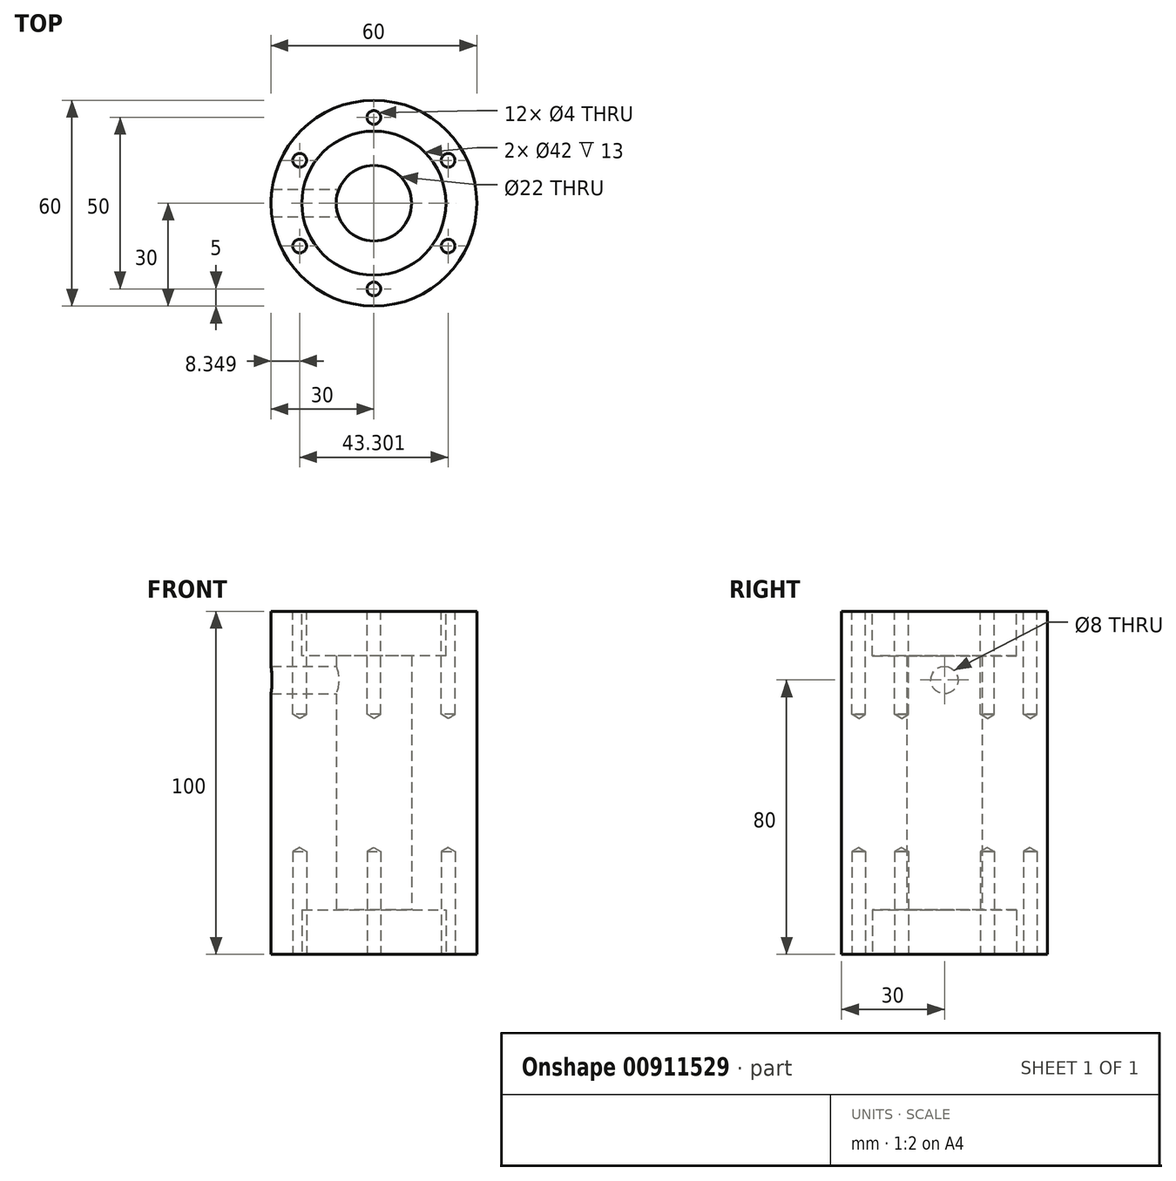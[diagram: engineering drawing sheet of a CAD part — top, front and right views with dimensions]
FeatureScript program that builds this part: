
annotation { "Feature Type Name" : "Feature", "Feature Type Description" : "" }
export const myFeature = defineFeature(function(context is Context, id is Id, definition is map)
    precondition{}
    {
        {
            var Q0;
            Q0=qCreatedBy(makeId("Top.planeOp"),FACE);
            var sketch = newSketch(context, id + "F0", { "sketchPlane" : qUnion([Q0])});
            skCircle(sketch, "E0", {"center": v(0, 0) * mm, "radius": 11 * mm});
            skCircle(sketch, "E1", {"center": v(0, 0) * mm, "radius": 30 * mm});
            skSolve(sketch);
        }
        {
            var Q0;
            Q0=makeQuery(id+"F0.imprint","IMPRINT",FACE,{"disambiguationData":[TD([[makeQuery(id+"F0.imprint","IMPRINT",EDGE,{"derivedFrom":sQuery(id+"F0.wireOp",EDGE,"E0")}),-1.0]])]});
            extrude(context, id + "F1", {"entities" : qUnion([Q0]), "depth" : 100 * mm, "offsetDistance" : 25 * mm});
        }
        {
            var Q0;
            Q0=makeQuery(id+"F1.opExtrude","CAP_FACE",FACE,{"disambiguationData":[OSD([sQuery(id+"F0.wireOp",EDGE,"E0"),sQuery(id+"F0.wireOp",EDGE,"E1")])],"isStart":false});
            var sketch = newSketch(context, id + "F2", { "sketchPlane" : qUnion([Q0])});
            skCircle(sketch, "E2", {"center": v(0, 0) * mm, "radius": 21 * mm});
            skCircle(sketch, "E3", {"center": v(0, 0) * mm, "radius": 11 * mm});
            skSolve(sketch);
        }
        {
            var Q0;
            Q0=makeQuery(id+"F2.imprint","IMPRINT",FACE,{"disambiguationData":[TD([[makeQuery(id+"F2.imprint","IMPRINT",EDGE,{"derivedFrom":sQuery(id+"F2.wireOp",EDGE,"E2")}),1.0]])]});
            extrude(context, id + "F3", {"entities" : qUnion([Q0]), "operationType" : NewBodyOperationType.REMOVE, "oppositeDirection" : true, "depth" : 13 * mm, "offsetDistance" : 25 * mm});
        }
        {
            var Q0;
            Q0=makeQuery(id+"F1.opExtrude","CAP_FACE",FACE,{"disambiguationData":[OSD([sQuery(id+"F0.wireOp",EDGE,"E0"),sQuery(id+"F0.wireOp",EDGE,"E1")])],"isStart":true});
            var sketch = newSketch(context, id + "F4", { "sketchPlane" : qUnion([Q0])});
            skCircle(sketch, "E4", {"center": v(0, 0) * mm, "radius": 21 * mm});
            skCircle(sketch, "E5", {"center": v(0, 0) * mm, "radius": 11 * mm});
            skSolve(sketch);
        }
        {
            var Q0;
            Q0=makeQuery(id+"F4.imprint","IMPRINT",FACE,{"disambiguationData":[TD([[makeQuery(id+"F4.imprint","IMPRINT",EDGE,{"derivedFrom":sQuery(id+"F4.wireOp",EDGE,"E4")}),1.0]])]});
            extrude(context, id + "F5", {"entities" : qUnion([Q0]), "operationType" : NewBodyOperationType.REMOVE, "oppositeDirection" : true, "depth" : 13 * mm, "offsetDistance" : 25 * mm});
        }
        {
            var Q0;
            Q0=qCreatedBy(makeId("Right.planeOp"),FACE);
            var sketch = newSketch(context, id + "F6", { "sketchPlane" : qUnion([Q0])});
            skPoint(sketch, "E6", {"position": v(0, 80) * mm});
            skSolve(sketch);
        }
        {
            var Q0;
            Q0=sQuery(id+"F6.wireOp",VERTEX,"E6");
            var Q1;
            Q1=makeQuery(id+"F1.opExtrude","SWEPT_BODY",BODY,{"disambiguationData":[OSD([sQuery(id+"F0.wireOp",EDGE,"E0"),sQuery(id+"F0.wireOp",EDGE,"E1")])]});
            hole(context, id + "F7", {"style" : HoleStyle.SIMPLE, "endStyle" : HoleEndStyle.THROUGH, "holeDiameter" : 8 * mm, "majorDiameter" : 5 * mm, "isTappedThrough" : true, "tappedDepth" : 12 * mm, "tapClearance" : 3, "locations" : qUnion([Q0]), "scope" : qUnion([Q1])});
        }
        {
            var Q0;
            Q0=makeQuery(id+"F1.opExtrude","CAP_FACE",FACE,{"disambiguationData":[OSD([sQuery(id+"F0.wireOp",EDGE,"E0"),sQuery(id+"F0.wireOp",EDGE,"E1")])],"isStart":false});
            var sketch = newSketch(context, id + "F8", { "sketchPlane" : qUnion([Q0])});
            skPoint(sketch, "E7", {"position": v(0, 25) * mm});
            skPoint(sketch, "E8.1.0", {"position": v(-21.65, 12.5) * mm});
            skPoint(sketch, "E8.2.0", {"position": v(-21.65, -12.5) * mm});
            skPoint(sketch, "E8.3.0", {"position": v(0, -25) * mm});
            skPoint(sketch, "E8.4.0", {"position": v(21.65, -12.5) * mm});
            skPoint(sketch, "E8.5.0", {"position": v(21.65, 12.5) * mm});
            skPoint(sketch, "E8.center", {"position": v(0, 0) * mm});
            skSolve(sketch);
        }
        {
            var Q0;
            Q0=sQuery(id+"F8.wireOp",VERTEX,"E7");
            var Q1;
            Q1=sQuery(id+"F8.wireOp",VERTEX,"E8.5.0");
            var Q2;
            Q2=sQuery(id+"F8.wireOp",VERTEX,"E8.4.0");
            var Q3;
            Q3=sQuery(id+"F8.wireOp",VERTEX,"E8.3.0");
            var Q4;
            Q4=sQuery(id+"F8.wireOp",VERTEX,"E8.2.0");
            var Q5;
            Q5=sQuery(id+"F8.wireOp",VERTEX,"E8.1.0");
            var Q6;
            Q6=makeQuery(id+"F1.opExtrude","SWEPT_BODY",BODY,{"disambiguationData":[OSD([sQuery(id+"F0.wireOp",EDGE,"E0"),sQuery(id+"F0.wireOp",EDGE,"E1")])]});
            hole(context, id + "F9", {"style" : HoleStyle.SIMPLE, "endStyle" : HoleEndStyle.BLIND, "holeDiameter" : 4 * mm, "majorDiameter" : 5 * mm, "holeDepth" : 30 * mm, "isTappedThrough" : true, "tappedDepth" : 12 * mm, "tapClearance" : 3, "locations" : qUnion([Q0, Q1, Q2, Q3, Q4, Q5]), "scope" : qUnion([Q6])});
        }
        {
            var Q0;
            Q0=makeQuery(id+"F1.opExtrude","CAP_FACE",FACE,{"disambiguationData":[OSD([sQuery(id+"F0.wireOp",EDGE,"E0"),sQuery(id+"F0.wireOp",EDGE,"E1")])],"isStart":true});
            var sketch = newSketch(context, id + "F10", { "sketchPlane" : qUnion([Q0])});
            skPoint(sketch, "E9", {"position": v(0, 25) * mm});
            skPoint(sketch, "E10.1.0", {"position": v(-21.65, 12.5) * mm});
            skPoint(sketch, "E10.2.0", {"position": v(-21.65, -12.5) * mm});
            skPoint(sketch, "E10.3.0", {"position": v(0, -25) * mm});
            skPoint(sketch, "E10.4.0", {"position": v(21.65, -12.5) * mm});
            skPoint(sketch, "E10.5.0", {"position": v(21.65, 12.5) * mm});
            skPoint(sketch, "E10.center", {"position": v(0, 0) * mm});
            skSolve(sketch);
        }
        {
            var Q0;
            Q0=sQuery(id+"F10.wireOp",VERTEX,"E9");
            var Q1;
            Q1=sQuery(id+"F10.wireOp",VERTEX,"E10.5.0");
            var Q2;
            Q2=sQuery(id+"F10.wireOp",VERTEX,"E10.4.0");
            var Q3;
            Q3=sQuery(id+"F10.wireOp",VERTEX,"E10.3.0");
            var Q4;
            Q4=sQuery(id+"F10.wireOp",VERTEX,"E10.2.0");
            var Q5;
            Q5=sQuery(id+"F10.wireOp",VERTEX,"E10.1.0");
            var Q6;
            Q6=makeQuery(id+"F1.opExtrude","SWEPT_BODY",BODY,{"disambiguationData":[OSD([sQuery(id+"F0.wireOp",EDGE,"E0"),sQuery(id+"F0.wireOp",EDGE,"E1")])]});
            hole(context, id + "F11", {"style" : HoleStyle.SIMPLE, "endStyle" : HoleEndStyle.BLIND, "holeDiameter" : 4 * mm, "majorDiameter" : 5 * mm, "holeDepth" : 30 * mm, "isTappedThrough" : true, "tappedDepth" : 12 * mm, "tapClearance" : 3, "locations" : qUnion([Q0, Q1, Q2, Q3, Q4, Q5]), "scope" : qUnion([Q6])});
        }
    });
